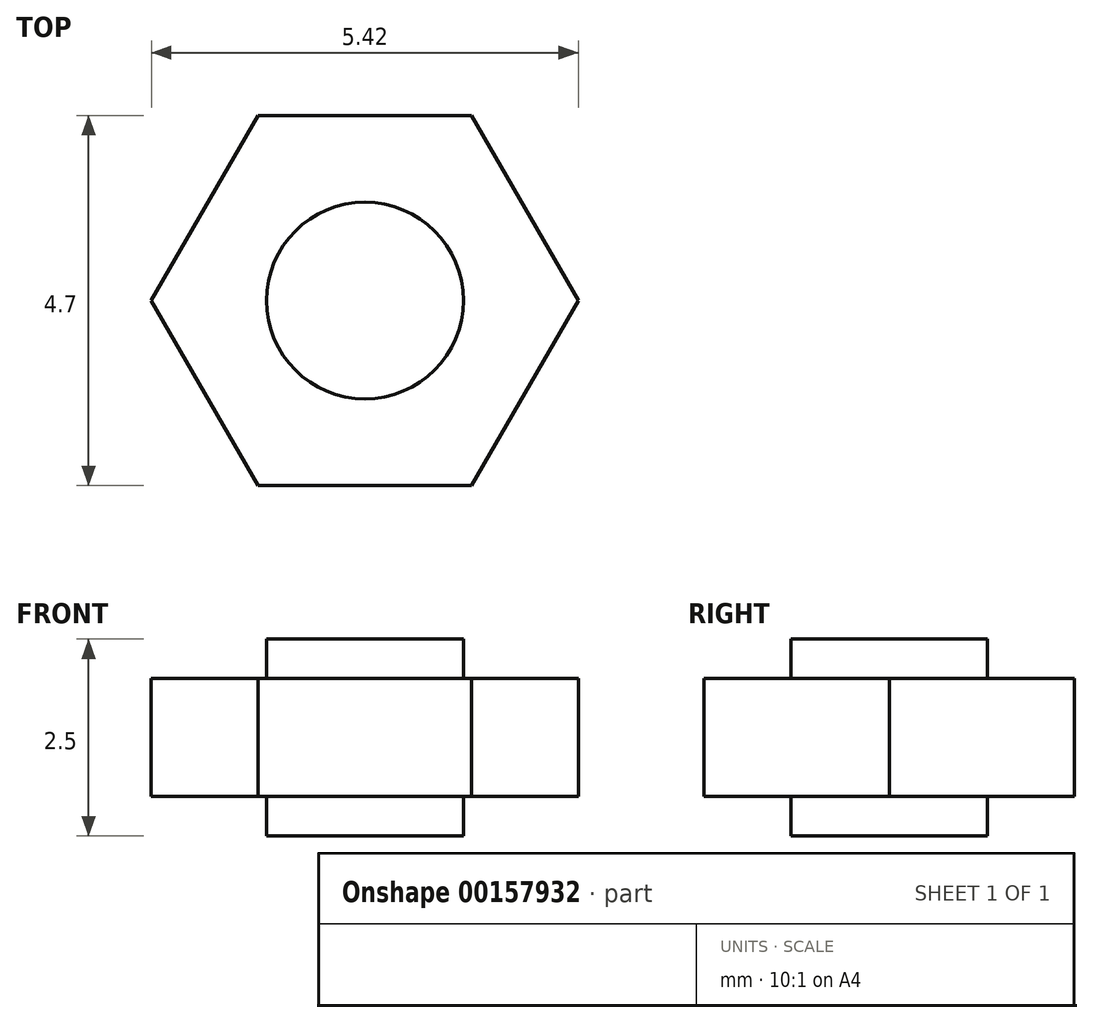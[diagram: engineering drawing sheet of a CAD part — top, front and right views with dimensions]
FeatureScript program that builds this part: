
annotation { "Feature Type Name" : "Feature", "Feature Type Description" : "" }
export const myFeature = defineFeature(function(context is Context, id is Id, definition is map)
    precondition{}
    {
        {
            assignVariable(context, id + "F0", {"name" : "h1", "anyValue" : 0.5});
        }
        {
            assignVariable(context, id + "F1", {"name" : "h2", "anyValue" : 1.5});
        }
        {
            var Q0;
            Q0=qCreatedBy(makeId("Top.planeOp"),FACE);
            var sketch = newSketch(context, id + "F2", { "sketchPlane" : qUnion([Q0])});
            skCircle(sketch, "E0.cCircle", {"center": v(0, 0) * mm, "radius": 2.35 * mm, "construction": true});
            skLineSegment(sketch, "E0.0", {"start": v(-1.36, 2.35) * mm, "end": v(1.36, 2.35) * mm});
            skLineSegment(sketch, "E0.1", {"start": v(1.36, 2.35) * mm, "end": v(2.71, 0) * mm});
            skLineSegment(sketch, "E0.2", {"start": v(2.71, 0) * mm, "end": v(1.36, -2.35) * mm});
            skLineSegment(sketch, "E0.3", {"start": v(1.36, -2.35) * mm, "end": v(-1.36, -2.35) * mm});
            skLineSegment(sketch, "E0.4", {"start": v(-1.36, -2.35) * mm, "end": v(-2.71, 0) * mm});
            skLineSegment(sketch, "E0.5", {"start": v(-2.71, 0) * mm, "end": v(-1.36, 2.35) * mm});
            skPoint(sketch, "E0.0.midPoint", {"position": v(0, 2.35) * mm});
            skCircle(sketch, "E1", {"center": v(0, 0) * mm, "radius": 1.25 * mm});
            skSolve(sketch);
        }
        {
            var Q0;
            Q0=makeQuery(id+"F2.imprint","IMPRINT",FACE,{"disambiguationData":[TD([[makeQuery(id+"F2.imprint","IMPRINT",EDGE,{"derivedFrom":sQuery(id+"F2.wireOp",EDGE,"E0.0")}),-1.0]])]});
            extrude(context, id + "F3", {"entities" : qUnion([Q0]), "depth" : (getVariable(context, 'h2')) * mm});
        }
        {
            var Q0;
            Q0=makeQuery(id+"F2.imprint","IMPRINT",FACE,{"disambiguationData":[TD([[makeQuery(id+"F2.imprint","IMPRINT",EDGE,{"derivedFrom":sQuery(id+"F2.wireOp",EDGE,"E1")}),1.0]])]});
            extrude(context, id + "F4", {"entities" : qUnion([Q0]), "operationType" : NewBodyOperationType.ADD, "oppositeDirection" : true, "depth" : (getVariable(context, 'h1')) * mm, "hasSecondDirection" : true, "secondDirectionOppositeDirection" : false, "secondDirectionDepth" : 2 * mm});
        }
    });
